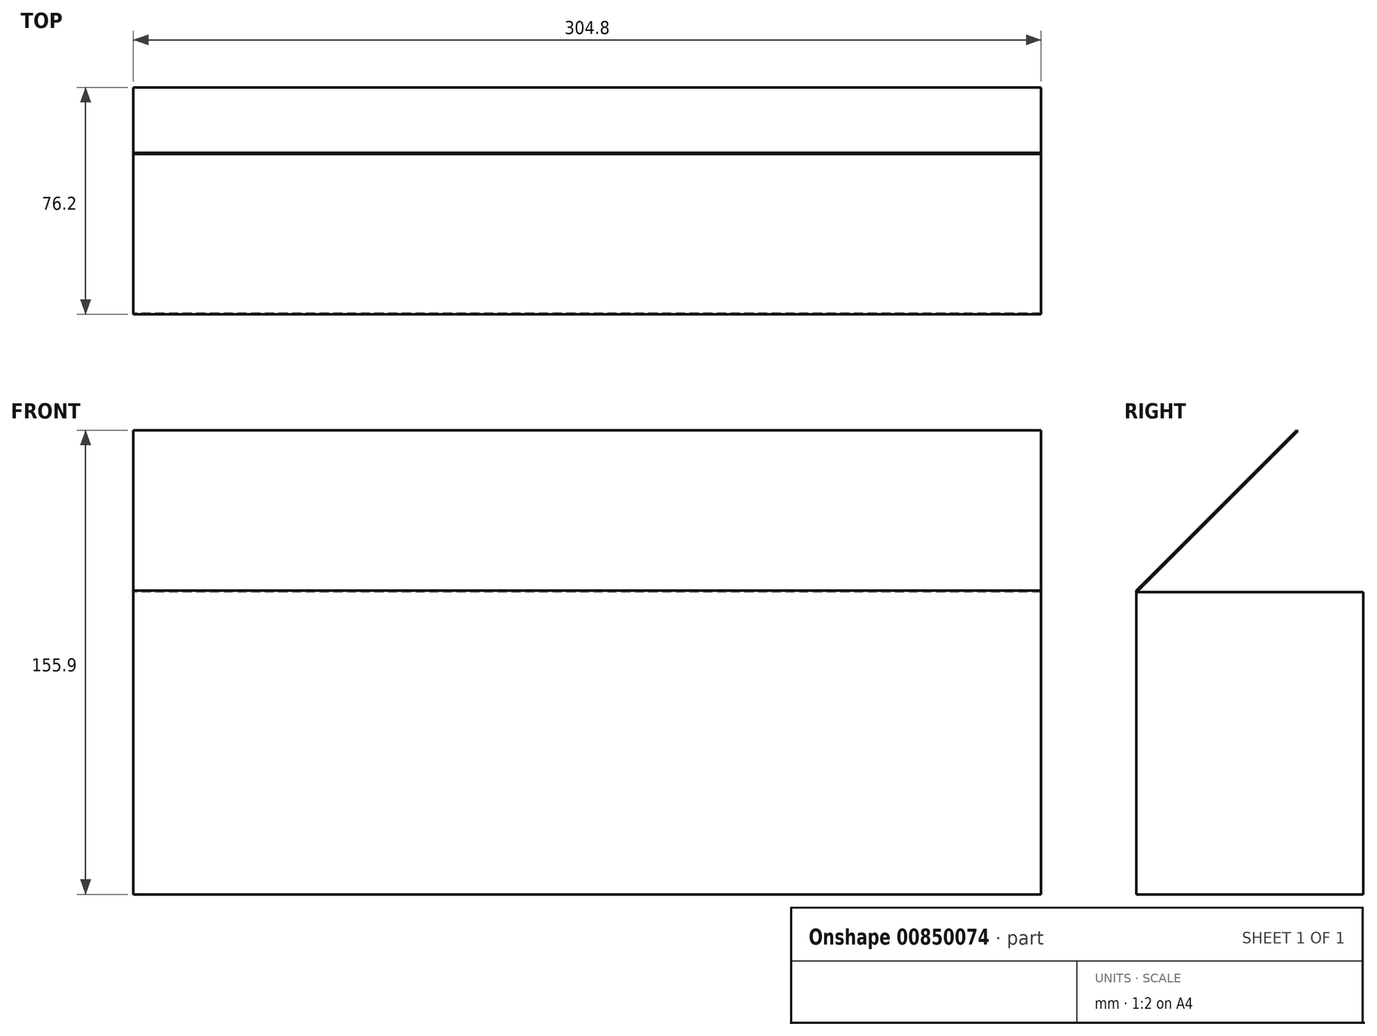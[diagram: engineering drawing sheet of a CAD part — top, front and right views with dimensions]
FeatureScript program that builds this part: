
annotation { "Feature Type Name" : "Feature", "Feature Type Description" : "" }
export const myFeature = defineFeature(function(context is Context, id is Id, definition is map)
    precondition{}
    {
        {
            var Q0;
            Q0=qCreatedBy(makeId("Right.planeOp"),FACE);
            var sketch = newSketch(context, id + "F0", { "sketchPlane" : qUnion([Q0])});
            skLineSegment(sketch, "E0.bottom", {"start": v(0, 0) * mm, "end": v(-76.2, 0) * mm});
            skLineSegment(sketch, "E0.top", {"start": v(0, 101.6) * mm, "end": v(-75.8, 101.6) * mm});
            skLineSegment(sketch, "E0.left", {"start": v(0, 0) * mm, "end": v(0, 101.6) * mm});
            skLineSegment(sketch, "E0.right", {"start": v(-76.2, 0) * mm, "end": v(-76.2, 102.02) * mm});
            skLineSegment(sketch, "E1", {"start": v(-76.2, 102.02) * mm, "end": v(-22.32, 155.9) * mm});
            skLineSegment(sketch, "E2", {"start": v(-22.32, 155.9) * mm, "end": v(-22.03, 155.62) * mm});
            skLineSegment(sketch, "E3", {"start": v(-22.03, 155.62) * mm, "end": v(-75.8, 101.85) * mm});
            skLineSegment(sketch, "E4", {"start": v(-75.8, 101.6) * mm, "end": v(-75.8, 101.85) * mm});
            skLineSegment(sketch, "E5", {"start": v(-75.8, 101.6) * mm, "end": v(-76.2, 101.6) * mm, "construction": true});
            skSolve(sketch);
        }
        {
            var Q0;
            Q0=qSketchRegion(id+"F0",true);
            extrude(context, id + "F1", {"entities" : qUnion([Q0]), "endBound" : BoundingType.SYMMETRIC, "depth" : 304.8 * mm, "offsetDistance" : 25.4 * mm});
        }
    });
